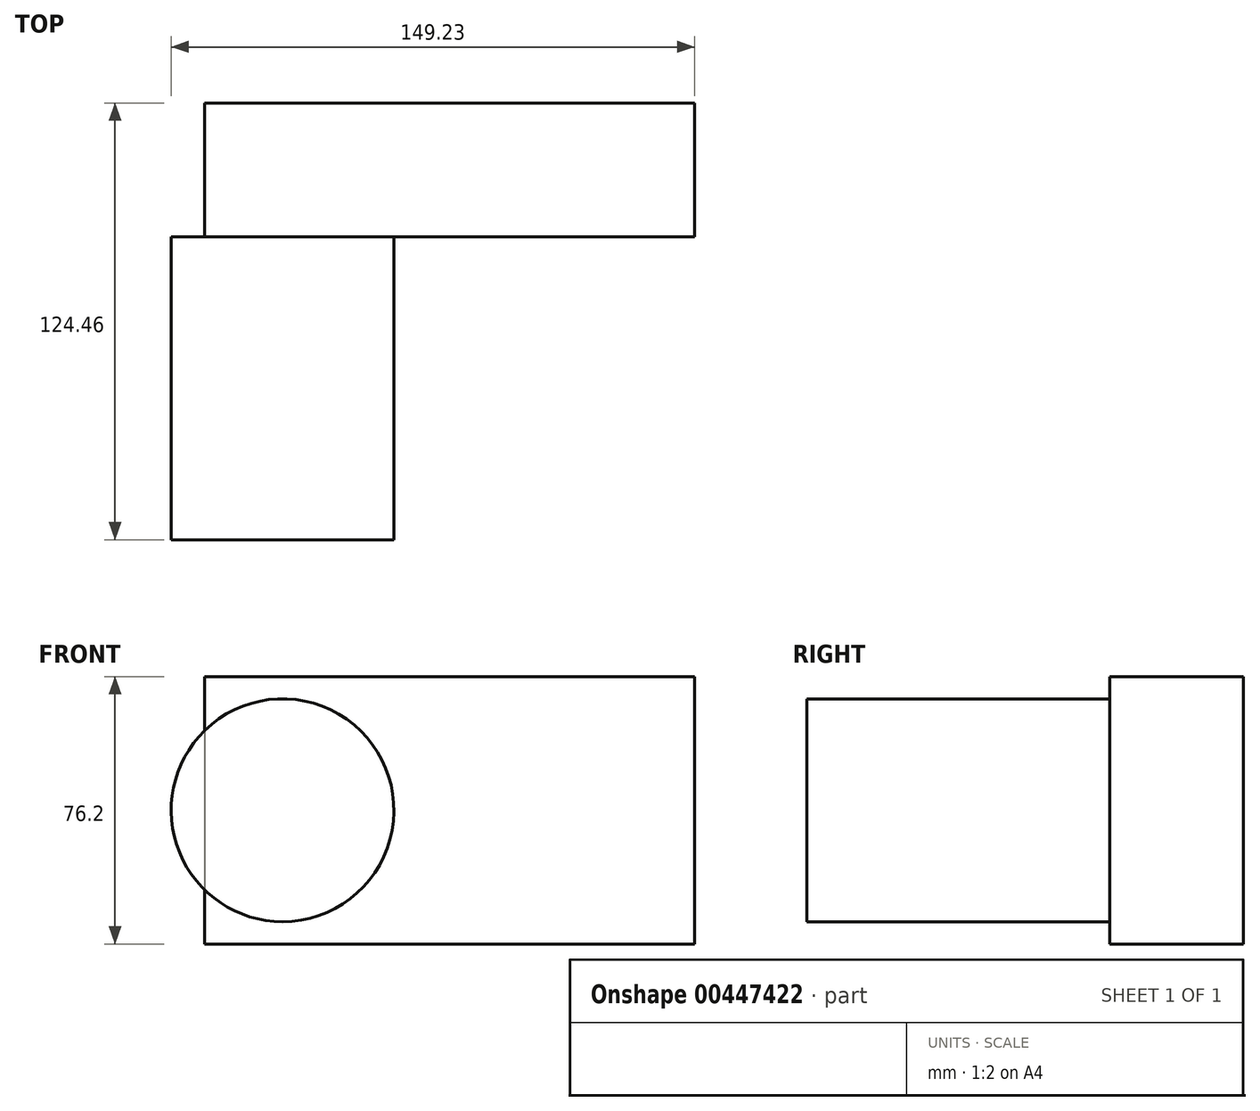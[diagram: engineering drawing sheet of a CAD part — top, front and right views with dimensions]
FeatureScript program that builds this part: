
annotation { "Feature Type Name" : "Feature", "Feature Type Description" : "" }
export const myFeature = defineFeature(function(context is Context, id is Id, definition is map)
    precondition{}
    {
        {
            var Q0;
            Q0=qCreatedBy(makeId("Top.planeOp"),FACE);
            var sketch = newSketch(context, id + "F0", { "sketchPlane" : qUnion([Q0])});
            skLineSegment(sketch, "E0.bottom", {"start": v(69.85, -19.05) * mm, "end": v(-69.85, -19.05) * mm});
            skLineSegment(sketch, "E0.top", {"start": v(69.85, 19.05) * mm, "end": v(-69.85, 19.05) * mm});
            skLineSegment(sketch, "E0.left", {"start": v(69.85, -19.05) * mm, "end": v(69.85, 19.05) * mm});
            skLineSegment(sketch, "E0.right", {"start": v(-69.85, -19.05) * mm, "end": v(-69.85, 19.05) * mm});
            skPoint(sketch, "E0.middle", {"position": v(0, 0) * mm});
            skPoint(sketch, "E1.middle.positionSnap0", {"position": v(0, 19.05) * mm});
            skPoint(sketch, "E1.cornerSnap0", {"position": v(0, -19.05) * mm});
            skPoint(sketch, "E1.centerSnap0", {"position": v(0, 19.05) * mm});
            skSolve(sketch);
        }
        {
            var Q0;
            Q0=makeQuery(id+"F0.imprint","IMPRINT",FACE,{"disambiguationData":[TD([[makeQuery(id+"F0.imprint","IMPRINT",EDGE,{"derivedFrom":sQuery(id+"F0.wireOp",EDGE,"E0.bottom")}),-1.0]])]});
            extrude(context, id + "F1", {"entities" : qUnion([Q0]), "depth" : 76.2 * mm});
        }
        {
            var Q0;
            Q0=makeQuery(id+"F1.opExtrude","SWEPT_FACE",FACE,{"disambiguationData":[OSD([sQuery(id+"F0.wireOp",EDGE,"E0.bottom")])]});
            var sketch = newSketch(context, id + "F2", { "sketchPlane" : qUnion([Q0])});
            skLineSegment(sketch, "E2", {"start": v(-47.63, 76.2) * mm, "end": v(-47.63, 0) * mm});
            skCircle(sketch, "E3", {"center": v(-47.63, 38.1) * mm, "radius": 31.75 * mm});
            skSolve(sketch);
        }
        {
            var Q0;
            {var subQ0=sQuery(id+"F2.wireOp",EDGE,"E3");var subQ1=sQuery(id+"F2.wireOp",EDGE,"E2");var subQ2=makeQuery(id+"F2.imprint","INTERSECT",VERTEX,{"disambiguationData":[OD(0.0)],"derivedFrom":[subQ1,subQ0]});Q0=makeQuery(id+"F2.imprint","IMPRINT",FACE,{"disambiguationData":[TD([[makeQuery(id+"F2.imprint","IMPRINT",EDGE,{"disambiguationData":[TD([[subQ2,-1.0]])],"derivedFrom":subQ1}),-1.0]])]});}
            var Q1;
            {var subQ0=sQuery(id+"F2.wireOp",EDGE,"E3");var subQ1=sQuery(id+"F2.wireOp",EDGE,"E2");var subQ2=makeQuery(id+"F2.imprint","INTERSECT",VERTEX,{"disambiguationData":[OD(0.0)],"derivedFrom":[subQ1,subQ0]});Q1=makeQuery(id+"F2.imprint","IMPRINT",FACE,{"disambiguationData":[TD([[makeQuery(id+"F2.imprint","IMPRINT",EDGE,{"disambiguationData":[TD([[subQ2,-1.0]])],"derivedFrom":subQ1}),1.0]])]});}
            var Q2;
            {var subQ0=sQuery(id+"F2.wireOp",EDGE,"E3");var subQ1=makeQuery(id+"F1.opExtrude","SWEPT_EDGE",EDGE,{"disambiguationData":[OSD([sQuery(id+"F0.wireOp",EDGE,"E0.bottom"),sQuery(id+"F0.wireOp",EDGE,"E0.right")])]});var subQ2=makeQuery(id+"F2.imprint","INTERSECT",VERTEX,{"disambiguationData":[OD(0.0)],"derivedFrom":[subQ1,subQ0]});Q2=makeQuery(id+"F2.imprint","IMPRINT",FACE,{"disambiguationData":[TD([[makeQuery(id+"F2.imprint","IMPRINT",EDGE,{"disambiguationData":[TD([[subQ2,-1.0]])],"derivedFrom":subQ0}),1.0]])]});}
            extrude(context, id + "F3", {"entities" : qUnion([Q0, Q1, Q2]), "operationType" : NewBodyOperationType.ADD, "depth" : 86.36 * mm});
        }
    });
